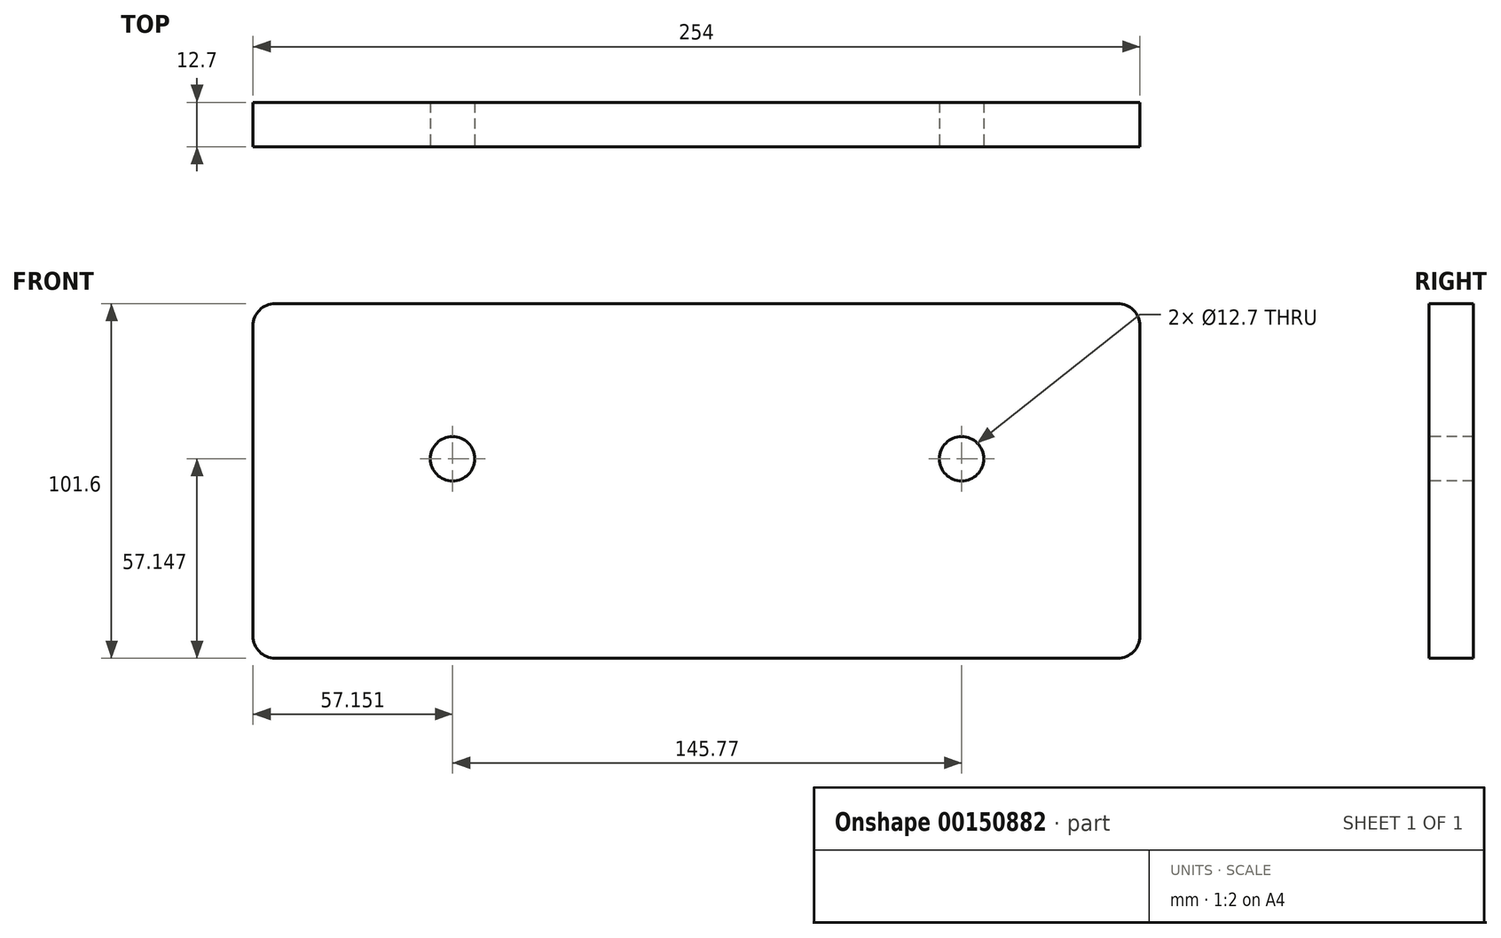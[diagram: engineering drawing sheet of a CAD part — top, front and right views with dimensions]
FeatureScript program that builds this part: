
annotation { "Feature Type Name" : "Feature", "Feature Type Description" : "" }
export const myFeature = defineFeature(function(context is Context, id is Id, definition is map)
    precondition{}
    {
        {
            var Q0;
            Q0=qCreatedBy(makeId("Front.planeOp"),FACE);
            var sketch = newSketch(context, id + "F0", { "sketchPlane" : qUnion([Q0])});
            skLineSegment(sketch, "E0.bottom", {"start": v(-58.88, 81.72) * mm, "end": v(195.12, 81.72) * mm});
            skLineSegment(sketch, "E0.top", {"start": v(-58.88, -19.88) * mm, "end": v(195.12, -19.88) * mm});
            skLineSegment(sketch, "E0.left", {"start": v(-58.88, 81.72) * mm, "end": v(-58.88, -19.88) * mm});
            skLineSegment(sketch, "E0.right", {"start": v(195.12, 81.72) * mm, "end": v(195.12, -19.88) * mm});
            skSolve(sketch);
        }
        {
            var Q0;
            Q0=makeQuery(id+"F0.imprint","IMPRINT",FACE,{"disambiguationData":[TD([[makeQuery(id+"F0.imprint","IMPRINT",EDGE,{"derivedFrom":sQuery(id+"F0.wireOp",EDGE,"E0.bottom")}),-1.0]])]});
            extrude(context, id + "F1", {"entities" : qUnion([Q0]), "depth" : 12.7 * mm});
        }
        {
            var Q0;
            Q0=makeQuery(id+"F1.opExtrude","SWEPT_EDGE",EDGE,{"disambiguationData":[OSD([sQuery(id+"F0.wireOp",EDGE,"E0.bottom"),sQuery(id+"F0.wireOp",EDGE,"E0.right")])]});
            var Q1;
            Q1=makeQuery(id+"F1.opExtrude","SWEPT_EDGE",EDGE,{"disambiguationData":[OSD([sQuery(id+"F0.wireOp",EDGE,"E0.bottom"),sQuery(id+"F0.wireOp",EDGE,"E0.left")])]});
            var Q2;
            Q2=makeQuery(id+"F1.opExtrude","SWEPT_EDGE",EDGE,{"disambiguationData":[OSD([sQuery(id+"F0.wireOp",EDGE,"E0.top"),sQuery(id+"F0.wireOp",EDGE,"E0.right")])]});
            var Q3;
            Q3=makeQuery(id+"F1.opExtrude","SWEPT_EDGE",EDGE,{"disambiguationData":[OSD([sQuery(id+"F0.wireOp",EDGE,"E0.top"),sQuery(id+"F0.wireOp",EDGE,"E0.left")])]});
            fillet(context, id + "F2", {"entities" : qUnion([Q0, Q1, Q2, Q3]), "radius" : 6.35 * mm, "tangentPropagation" : true, "allowEdgeOverflow" : false});
        }
        {
            var Q0;
            Q0=makeQuery(id+"F1.opExtrude","CAP_FACE",FACE,{"disambiguationData":[OSD([sQuery(id+"F0.wireOp",EDGE,"E0.bottom"),sQuery(id+"F0.wireOp",EDGE,"E0.top"),sQuery(id+"F0.wireOp",EDGE,"E0.left"),sQuery(id+"F0.wireOp",EDGE,"E0.right")])],"isStart":false});
            var sketch = newSketch(context, id + "F3", { "sketchPlane" : qUnion([Q0])});
            skCircle(sketch, "E1", {"center": v(-1.73, 37.27) * mm, "radius": 6.35 * mm});
            skCircle(sketch, "E2", {"center": v(144.04, 37.27) * mm, "radius": 6.35 * mm});
            skSolve(sketch);
        }
        {
            var Q0;
            Q0 = qSketchRegion(id + "F3", true);
            extrude(context, id + "F4", {"entities" : qUnion([Q0]), "operationType" : NewBodyOperationType.REMOVE, "oppositeDirection" : true, "depth" : 203.2 * mm});
        }
    });
